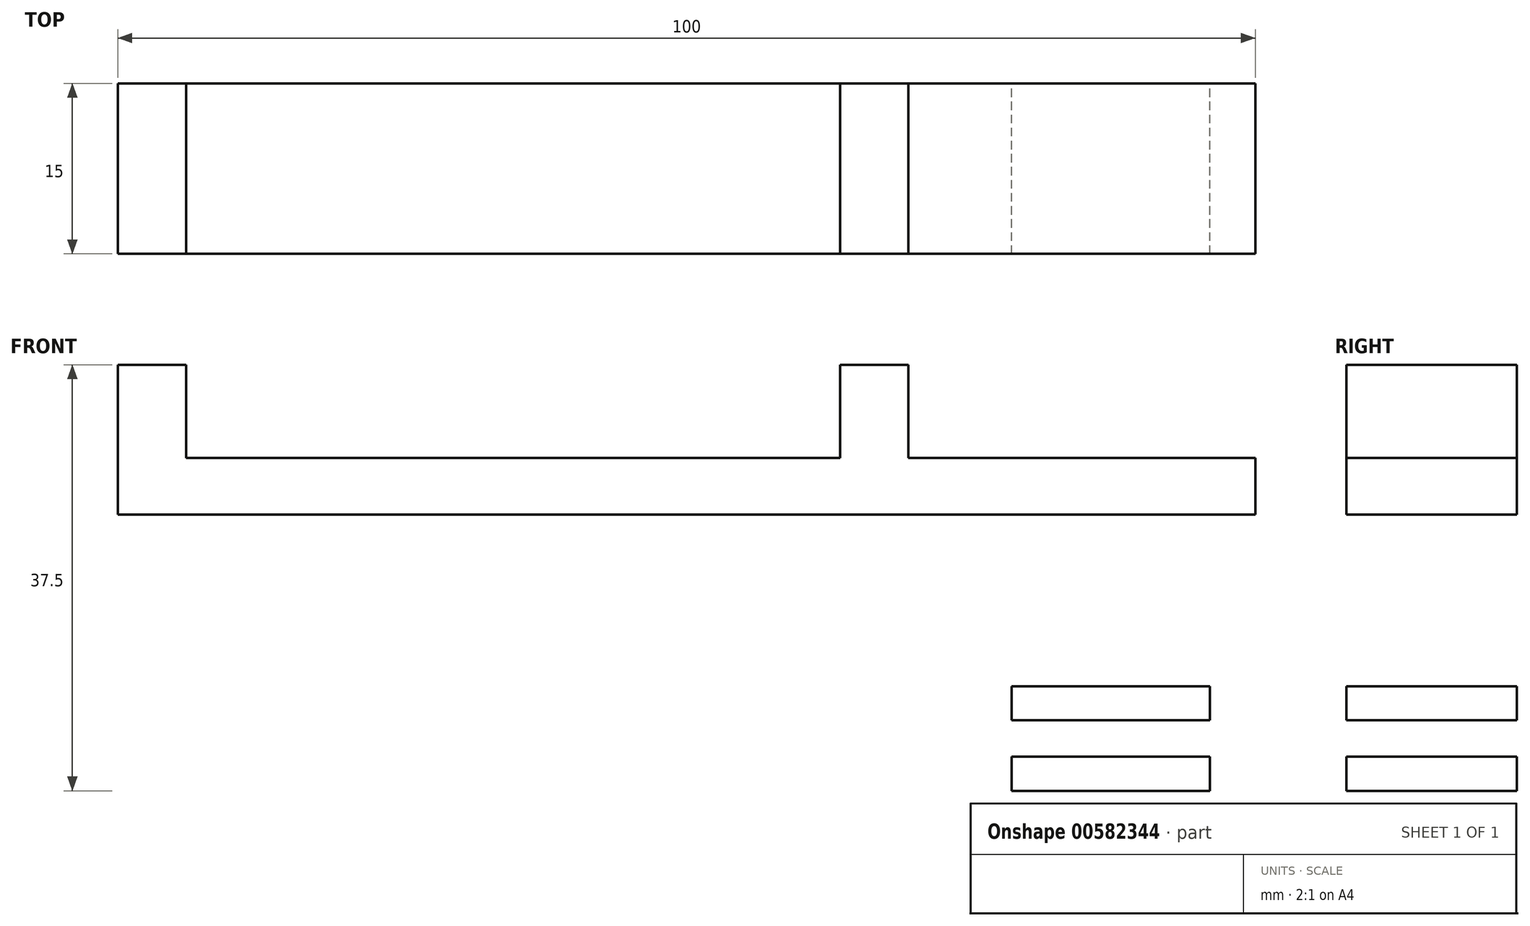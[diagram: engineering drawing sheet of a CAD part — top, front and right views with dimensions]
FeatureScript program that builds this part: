
annotation { "Feature Type Name" : "Feature", "Feature Type Description" : "" }
export const myFeature = defineFeature(function(context is Context, id is Id, definition is map)
    precondition{}
    {
        {
            var Q0;
            Q0=qCreatedBy(makeId("Front.planeOp"),FACE);
            var sketch = newSketch(context, id + "F0", { "sketchPlane" : qUnion([Q0])});
            skLineSegment(sketch, "E0.top", {"start": v(-49.91, 9.81) * mm, "end": v(50.09, 9.81) * mm});
            skLineSegment(sketch, "E0.left", {"start": v(-49.91, 14.81) * mm, "end": v(-49.91, 9.81) * mm});
            skLineSegment(sketch, "E0.right", {"start": v(50.09, 14.81) * mm, "end": v(50.09, 9.81) * mm});
            skLineSegment(sketch, "E1.bottom", {"start": v(50.09, 9.81) * mm, "end": v(46.09, 9.81) * mm});
            skLineSegment(sketch, "E1.top", {"start": v(50.09, -14.49) * mm, "end": v(46.09, -14.49) * mm});
            skLineSegment(sketch, "E1.left", {"start": v(50.09, 9.81) * mm, "end": v(50.09, -14.49) * mm});
            skLineSegment(sketch, "E2.bottom", {"start": v(46.09, -14.49) * mm, "end": v(28.69, -14.49) * mm});
            skLineSegment(sketch, "E2.top", {"start": v(46.09, -11.49) * mm, "end": v(28.69, -11.49) * mm});
            skLineSegment(sketch, "E2.left", {"start": v(46.09, -14.49) * mm, "end": v(46.09, -11.49) * mm});
            skLineSegment(sketch, "E2.right", {"start": v(28.69, -14.49) * mm, "end": v(28.69, -11.49) * mm});
            skLineSegment(sketch, "E3.bottom", {"start": v(-49.91, 14.81) * mm, "end": v(-43.91, 14.81) * mm});
            skLineSegment(sketch, "E3.top", {"start": v(-49.91, 23.01) * mm, "end": v(-43.91, 23.01) * mm});
            skLineSegment(sketch, "E3.left", {"start": v(-49.91, 14.81) * mm, "end": v(-49.91, 23.01) * mm});
            skLineSegment(sketch, "E3.right", {"start": v(-43.91, 14.81) * mm, "end": v(-43.91, 23.01) * mm});
            skLineSegment(sketch, "E4.bottom", {"start": v(13.59, 14.81) * mm, "end": v(19.59, 14.81) * mm});
            skLineSegment(sketch, "E4.top", {"start": v(13.59, 23.01) * mm, "end": v(19.59, 23.01) * mm});
            skLineSegment(sketch, "E4.left", {"start": v(13.59, 14.81) * mm, "end": v(13.59, 23.01) * mm});
            skLineSegment(sketch, "E4.right", {"start": v(19.59, 14.81) * mm, "end": v(19.59, 23.01) * mm});
            skLineSegment(sketch, "E5.bottom", {"start": v(46.09, -5.29) * mm, "end": v(28.69, -5.29) * mm});
            skLineSegment(sketch, "E5.top", {"start": v(46.09, -8.29) * mm, "end": v(28.69, -8.29) * mm});
            skLineSegment(sketch, "E5.left", {"start": v(46.09, -5.29) * mm, "end": v(46.09, -8.29) * mm});
            skLineSegment(sketch, "E5.right", {"start": v(28.69, -5.29) * mm, "end": v(28.69, -8.29) * mm});
            skLineSegment(sketch, "E6", {"start": v(-43.91, 14.81) * mm, "end": v(13.59, 14.81) * mm});
            skLineSegment(sketch, "E7", {"start": v(19.59, 14.81) * mm, "end": v(50.09, 14.81) * mm});
            skLineSegment(sketch, "E8", {"start": v(46.09, 9.81) * mm, "end": v(46.09, -5.29) * mm});
            skLineSegment(sketch, "E9", {"start": v(46.09, -8.29) * mm, "end": v(46.09, -11.49) * mm});
            skSolve(sketch);
        }
        {
            var Q0;
            Q0=makeQuery(id+"F0.imprint","IMPRINT",FACE,{"disambiguationData":[TD([[makeQuery(id+"F0.imprint","IMPRINT",EDGE,{"derivedFrom":sQuery(id+"F0.wireOp",EDGE,"E0.top")}),1.0]])]});
            var Q1;
            Q1=makeQuery(id+"F0.imprint","IMPRINT",FACE,{"disambiguationData":[TD([[makeQuery(id+"F0.imprint","IMPRINT",EDGE,{"derivedFrom":sQuery(id+"F0.wireOp",EDGE,"E4.bottom")}),1.0]])]});
            var Q2;
            Q2=makeQuery(id+"F0.imprint","IMPRINT",FACE,{"disambiguationData":[TD([[makeQuery(id+"F0.imprint","IMPRINT",EDGE,{"derivedFrom":sQuery(id+"F0.wireOp",EDGE,"E3.bottom")}),1.0]])]});
            var Q3;
            Q3=makeQuery(id+"F0.imprint","IMPRINT",FACE,{"disambiguationData":[TD([[makeQuery(id+"F0.imprint","IMPRINT",EDGE,{"derivedFrom":sQuery(id+"F0.wireOp",EDGE,"E1.bottom")}),1.0]])]});
            var Q4;
            Q4=makeQuery(id+"F0.imprint","IMPRINT",FACE,{"disambiguationData":[TD([[makeQuery(id+"F0.imprint","IMPRINT",EDGE,{"derivedFrom":sQuery(id+"F0.wireOp",EDGE,"E5.bottom")}),1.0]])]});
            var Q5;
            Q5=makeQuery(id+"F0.imprint","IMPRINT",FACE,{"disambiguationData":[TD([[makeQuery(id+"F0.imprint","IMPRINT",EDGE,{"derivedFrom":sQuery(id+"F0.wireOp",EDGE,"E2.bottom")}),-1.0]])]});
            extrude(context, id + "F1", {"entities" : qUnion([Q0, Q1, Q2, Q3, Q4, Q5]), "endBound" : BoundingType.SYMMETRIC, "depth" : 15 * mm, "offsetDistance" : 25 * mm});
        }
    });
